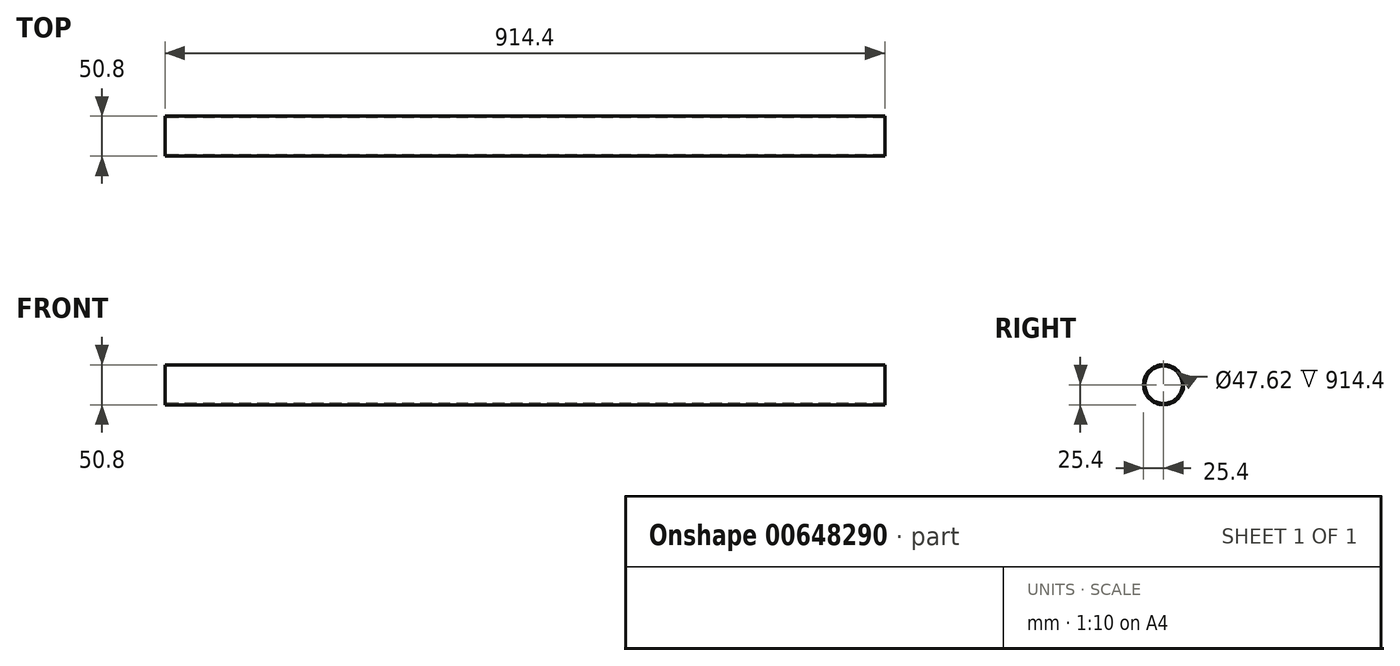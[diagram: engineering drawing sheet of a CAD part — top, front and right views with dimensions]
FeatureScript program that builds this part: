
annotation { "Feature Type Name" : "Feature", "Feature Type Description" : "" }
export const myFeature = defineFeature(function(context is Context, id is Id, definition is map)
    precondition{}
    {
        {
            var Q0;
            Q0=qCreatedBy(makeId("Right.planeOp"),FACE);
            var sketch = newSketch(context, id + "F0", { "sketchPlane" : qUnion([Q0])});
            skCircle(sketch, "E0", {"center": v(0, 0) * mm, "radius": 25.4 * mm});
            skCircle(sketch, "E1.0", {"center": v(0, 0) * mm, "radius": 23.81 * mm});
            skSolve(sketch);
        }
        {
            var Q0;
            Q0=makeQuery(id+"F0.imprint","IMPRINT",FACE,{"disambiguationData":[TD([[makeQuery(id+"F0.imprint","IMPRINT",EDGE,{"derivedFrom":sQuery(id+"F0.wireOp",EDGE,"E0")}),1.0]])]});
            extrude(context, id + "F1", {"entities" : qUnion([Q0]), "depth" : 457.2 * mm, "offsetDistance" : 25.4 * mm, "hasSecondDirection" : true, "secondDirectionOppositeDirection" : true, "secondDirectionDepth" : 457.2 * mm});
        }
    });
